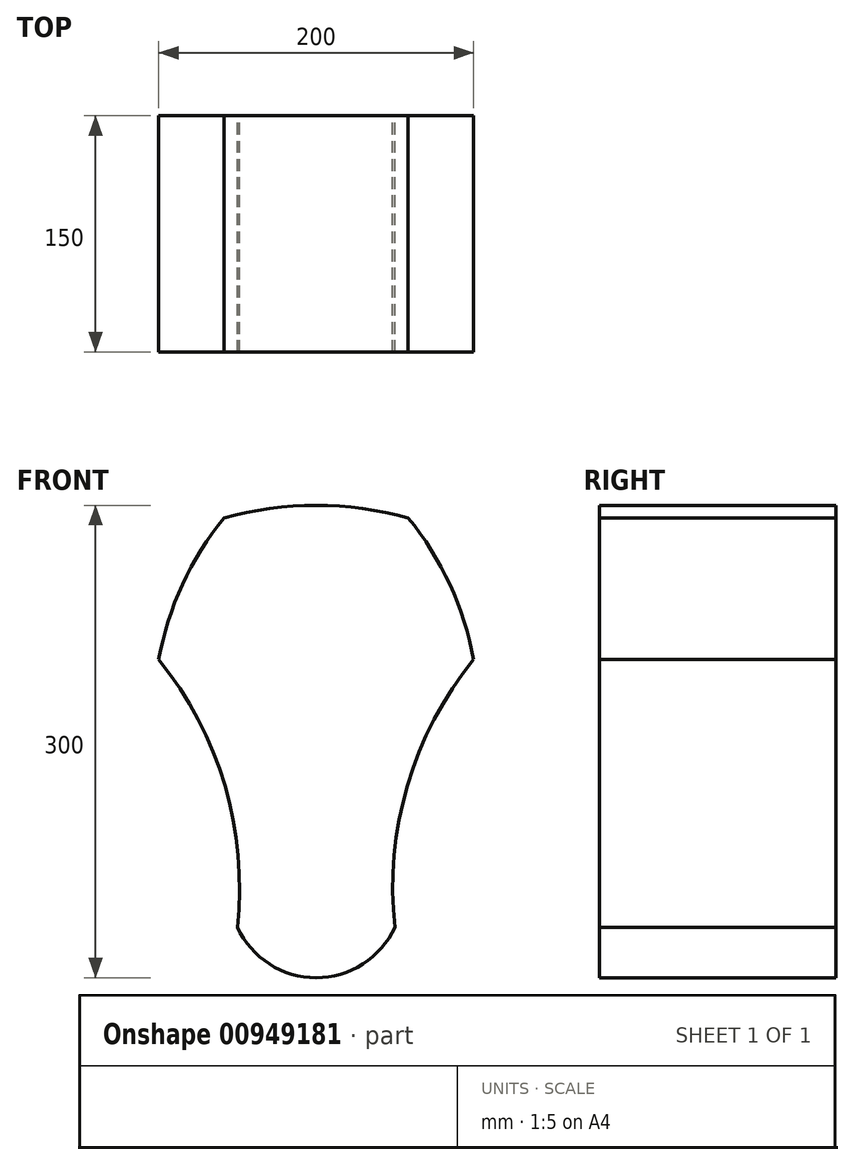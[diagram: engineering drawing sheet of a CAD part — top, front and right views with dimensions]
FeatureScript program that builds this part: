
annotation { "Feature Type Name" : "Feature", "Feature Type Description" : "" }
export const myFeature = defineFeature(function(context is Context, id is Id, definition is map)
    precondition{}
    {
        {
            var Q0;
            Q0=qCreatedBy(makeId("Front.planeOp"),FACE);
            var sketch = newSketch(context, id + "F0", { "sketchPlane" : qUnion([Q0])});
            skLineSegment(sketch, "E0", {"start": v(0, 0) * mm, "end": v(0, 300) * mm, "construction": true});
            skArc(sketch, "E1", {"start": v(58.47, 292.09) * mm, "mid": v(29.5, 298.01) * mm, "end": v(0, 300) * mm});
            skLineSegment(sketch, "E2", {"start": v(0, 300) * mm, "end": v(-15.5, 300) * mm, "construction": true});
            skArc(sketch, "E3.MirrorCS", {"start": v(-58.47, 292.09) * mm, "mid": v(-29.5, 298.01) * mm, "end": v(0, 300) * mm});
            skArc(sketch, "E4", {"start": v(100, 202.09) * mm, "mid": v(84.9, 249.7) * mm, "end": v(58.47, 292.09) * mm});
            skArc(sketch, "E5", {"start": v(100, 202.09) * mm, "mid": v(57.97, 122.1) * mm, "end": v(50, 32.09) * mm});
            skArc(sketch, "E6", {"start": v(0, 0) * mm, "mid": v(29.7, 8.71) * mm, "end": v(50, 32.09) * mm});
            skArc(sketch, "E7.MirrorCS", {"start": v(-100, 202.09) * mm, "mid": v(-57.97, 122.1) * mm, "end": v(-50, 32.09) * mm});
            skArc(sketch, "E8.MirrorCS", {"start": v(0, 0) * mm, "mid": v(-29.7, 8.71) * mm, "end": v(-50, 32.09) * mm});
            skArc(sketch, "E9.MirrorCS", {"start": v(-100, 202.09) * mm, "mid": v(-84.9, 249.7) * mm, "end": v(-58.47, 292.09) * mm});
            skSolve(sketch);
        }
        {
            var Q0;
            Q0 = qSketchRegion(id + "F0", true);
            extrude(context, id + "F1", {"entities" : qUnion([Q0]), "depth" : 150 * mm, "offsetDistance" : 25 * mm});
        }
    });
